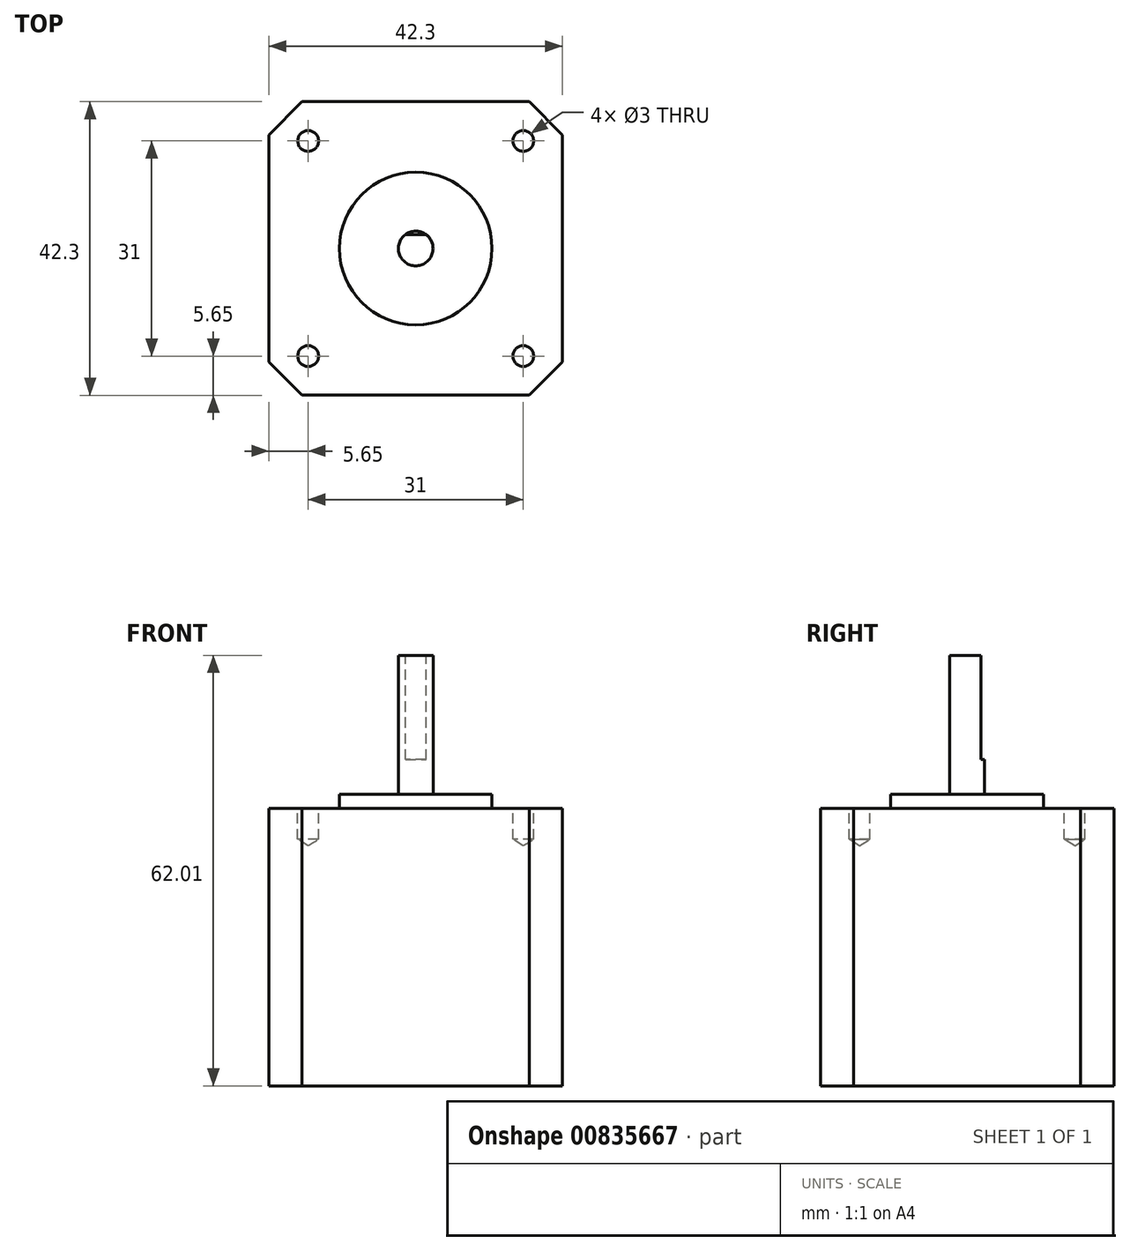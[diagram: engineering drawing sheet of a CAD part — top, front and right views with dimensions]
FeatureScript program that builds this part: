
annotation { "Feature Type Name" : "Feature", "Feature Type Description" : "" }
export const myFeature = defineFeature(function(context is Context, id is Id, definition is map)
    precondition{}
    {
        {
            var Q0;
            Q0=qCreatedBy(makeId("Top.planeOp"),FACE);
            var sketch = newSketch(context, id + "F0", { "sketchPlane" : qUnion([Q0])});
            skLineSegment(sketch, "E0.bottom", {"start": v(-21.15, 21.15) * mm, "end": v(21.15, 21.15) * mm});
            skLineSegment(sketch, "E0.top", {"start": v(-21.15, -21.15) * mm, "end": v(21.15, -21.15) * mm});
            skLineSegment(sketch, "E0.left", {"start": v(-21.15, 21.15) * mm, "end": v(-21.15, -21.15) * mm});
            skLineSegment(sketch, "E0.right", {"start": v(21.15, 21.15) * mm, "end": v(21.15, -21.15) * mm});
            skLineSegment(sketch, "E1", {"start": v(-21.15, 21.15) * mm, "end": v(21.15, -21.15) * mm, "construction": true});
            skSolve(sketch);
        }
        {
            var Q0;
            Q0=makeQuery(id+"F0.imprint","IMPRINT",FACE,{"disambiguationData":[TD([[makeQuery(id+"F0.imprint","IMPRINT",EDGE,{"derivedFrom":sQuery(id+"F0.wireOp",EDGE,"E0.bottom")}),-1.0]])]});
            extrude(context, id + "F1", {"entities" : qUnion([Q0]), "depth" : 40 * mm, "offsetDistance" : 25.4 * mm});
        }
        {
            var Q0;
            Q0=makeQuery(id+"F1.opExtrude","SWEPT_EDGE",EDGE,{"disambiguationData":[OSD([sQuery(id+"F0.wireOp",EDGE,"E0.top"),sQuery(id+"F0.wireOp",EDGE,"E0.right")])]});
            var Q1;
            Q1=makeQuery(id+"F1.opExtrude","SWEPT_EDGE",EDGE,{"disambiguationData":[OSD([sQuery(id+"F0.wireOp",EDGE,"E0.bottom"),sQuery(id+"F0.wireOp",EDGE,"E0.right")])]});
            var Q2;
            Q2=makeQuery(id+"F1.opExtrude","SWEPT_EDGE",EDGE,{"disambiguationData":[OSD([sQuery(id+"F0.wireOp",EDGE,"E0.bottom"),sQuery(id+"F0.wireOp",EDGE,"E0.left")])]});
            var Q3;
            Q3=makeQuery(id+"F1.opExtrude","SWEPT_EDGE",EDGE,{"disambiguationData":[OSD([sQuery(id+"F0.wireOp",EDGE,"E0.top"),sQuery(id+"F0.wireOp",EDGE,"E0.left")])]});
            chamfer(context, id + "F2", {"entities" : qUnion([Q0, Q1, Q2, Q3]), "width" : 4.78 * mm, "tangentPropagation" : true});
        }
        {
            var Q0;
            Q0=makeQuery(id+"F1.opExtrude","CAP_FACE",FACE,{"disambiguationData":[OSD([sQuery(id+"F0.wireOp",EDGE,"E0.bottom"),sQuery(id+"F0.wireOp",EDGE,"E0.top"),sQuery(id+"F0.wireOp",EDGE,"E0.left"),sQuery(id+"F0.wireOp",EDGE,"E0.right")])],"isStart":false});
            var sketch = newSketch(context, id + "F3", { "sketchPlane" : qUnion([Q0])});
            skCircle(sketch, "E2", {"center": v(0, 0) * mm, "radius": 11 * mm});
            skSolve(sketch);
        }
        {
            var Q0;
            Q0=makeQuery(id+"F3.imprint","IMPRINT",FACE,{"disambiguationData":[TD([[makeQuery(id+"F3.imprint","IMPRINT",EDGE,{"derivedFrom":sQuery(id+"F3.wireOp",EDGE,"E2")}),1.0]])]});
            var Q1;
            Q1=sQuery(id+"F3.wireOp",EDGE,"E2");
            extrude(context, id + "F4", {"entities" : qUnion([Q0]), "operationType" : NewBodyOperationType.ADD, "surfaceEntities" : qUnion([Q1]), "depth" : 2 * mm, "offsetDistance" : 25.4 * mm});
        }
        {
            var Q0;
            Q0=makeQuery(id+"F1.opExtrude","CAP_FACE",FACE,{"disambiguationData":[OSD([sQuery(id+"F0.wireOp",EDGE,"E0.bottom"),sQuery(id+"F0.wireOp",EDGE,"E0.top"),sQuery(id+"F0.wireOp",EDGE,"E0.left"),sQuery(id+"F0.wireOp",EDGE,"E0.right")])],"isStart":false});
            var sketch = newSketch(context, id + "F5", { "sketchPlane" : qUnion([Q0])});
            skCircle(sketch, "E3", {"center": v(0, 0) * mm, "radius": 2.5 * mm});
            skSolve(sketch);
        }
        {
            var Q0;
            Q0 = qSketchRegion(id + "F5", true);
            extrude(context, id + "F6", {"entities" : qUnion([Q0]), "operationType" : NewBodyOperationType.ADD, "depth" : 22 * mm, "offsetDistance" : 25.4 * mm});
        }
        {
            var Q0;
            Q0=makeQuery(id+"F6.opExtrude","CAP_FACE",FACE,{"disambiguationData":[OSD([sQuery(id+"F5.wireOp",EDGE,"E3")])],"isStart":false});
            var sketch = newSketch(context, id + "F7", { "sketchPlane" : qUnion([Q0])});
            skLineSegment(sketch, "E4.bottom", {"start": v(-1.5, 2.5) * mm, "end": v(1.5, 2.5) * mm});
            skLineSegment(sketch, "E4.top", {"start": v(-1.5, 2) * mm, "end": v(1.5, 2) * mm});
            skLineSegment(sketch, "E4.left", {"start": v(-1.5, 2.5) * mm, "end": v(-1.5, 2) * mm});
            skLineSegment(sketch, "E4.right", {"start": v(1.5, 2.5) * mm, "end": v(1.5, 2) * mm});
            skLineSegment(sketch, "E5", {"start": v(0, 2.5) * mm, "end": v(0, 0) * mm, "construction": true});
            skSolve(sketch);
        }
        {
            var Q0;
            {var subQ0=sQuery(id+"F7.wireOp",EDGE,"E4.top");Q0=makeQuery(id+"F7.imprint","IMPRINT",FACE,{"disambiguationData":[TD([[makeQuery(id+"F7.imprint","IMPRINT",EDGE,{"derivedFrom":subQ0}),1.0]])]});}
            extrude(context, id + "F8", {"entities" : qUnion([Q0]), "operationType" : NewBodyOperationType.REMOVE, "oppositeDirection" : true, "depth" : 15 * mm, "offsetDistance" : 25.4 * mm});
        }
        {
            var Q0;
            Q0=makeQuery(id+"F1.opExtrude","CAP_FACE",FACE,{"disambiguationData":[OSD([sQuery(id+"F0.wireOp",EDGE,"E0.bottom"),sQuery(id+"F0.wireOp",EDGE,"E0.top"),sQuery(id+"F0.wireOp",EDGE,"E0.left"),sQuery(id+"F0.wireOp",EDGE,"E0.right")])],"isStart":false});
            var sketch = newSketch(context, id + "F9", { "sketchPlane" : qUnion([Q0])});
            skLineSegment(sketch, "E6.bottom", {"start": v(-15.5, 15.5) * mm, "end": v(15.5, 15.5) * mm, "construction": true});
            skLineSegment(sketch, "E6.top", {"start": v(-15.5, -15.5) * mm, "end": v(15.5, -15.5) * mm, "construction": true});
            skLineSegment(sketch, "E6.left", {"start": v(-15.5, 15.5) * mm, "end": v(-15.5, -15.5) * mm, "construction": true});
            skLineSegment(sketch, "E6.right", {"start": v(15.5, 15.5) * mm, "end": v(15.5, -15.5) * mm, "construction": true});
            skLineSegment(sketch, "E7", {"start": v(-15.5, -15.5) * mm, "end": v(15.5, 15.5) * mm, "construction": true});
            skPoint(sketch, "E8", {"position": v(-15.5, 15.5) * mm});
            skPoint(sketch, "E9", {"position": v(15.5, 15.5) * mm});
            skPoint(sketch, "E10", {"position": v(15.5, -15.5) * mm});
            skPoint(sketch, "E11", {"position": v(-15.5, -15.5) * mm});
            skSolve(sketch);
        }
        {
            var Q0;
            Q0=sQuery(id+"F9.wireOp",VERTEX,"E8");
            var Q1;
            Q1=sQuery(id+"F9.wireOp",VERTEX,"E11");
            var Q2;
            Q2=sQuery(id+"F9.wireOp",VERTEX,"E10");
            var Q3;
            Q3=sQuery(id+"F9.wireOp",VERTEX,"E9");
            var Q4;
            Q4=makeQuery(id+"F1.opExtrude","SWEPT_BODY",BODY,{"disambiguationData":[OSD([sQuery(id+"F0.wireOp",EDGE,"E0.bottom"),sQuery(id+"F0.wireOp",EDGE,"E0.top"),sQuery(id+"F0.wireOp",EDGE,"E0.left"),sQuery(id+"F0.wireOp",EDGE,"E0.right")])]});
            hole(context, id + "F10", {"style" : HoleStyle.SIMPLE, "endStyle" : HoleEndStyle.BLIND, "holeDiameter" : 3 * mm, "majorDiameter" : 6.35 * mm, "holeDepth" : 4.5 * mm, "isTappedThrough" : true, "tappedDepth" : 12.7 * mm, "tapClearance" : 3, "startFromSketch" : true, "locations" : qUnion([Q0, Q1, Q2, Q3]), "scope" : qUnion([Q4])});
        }
    });
